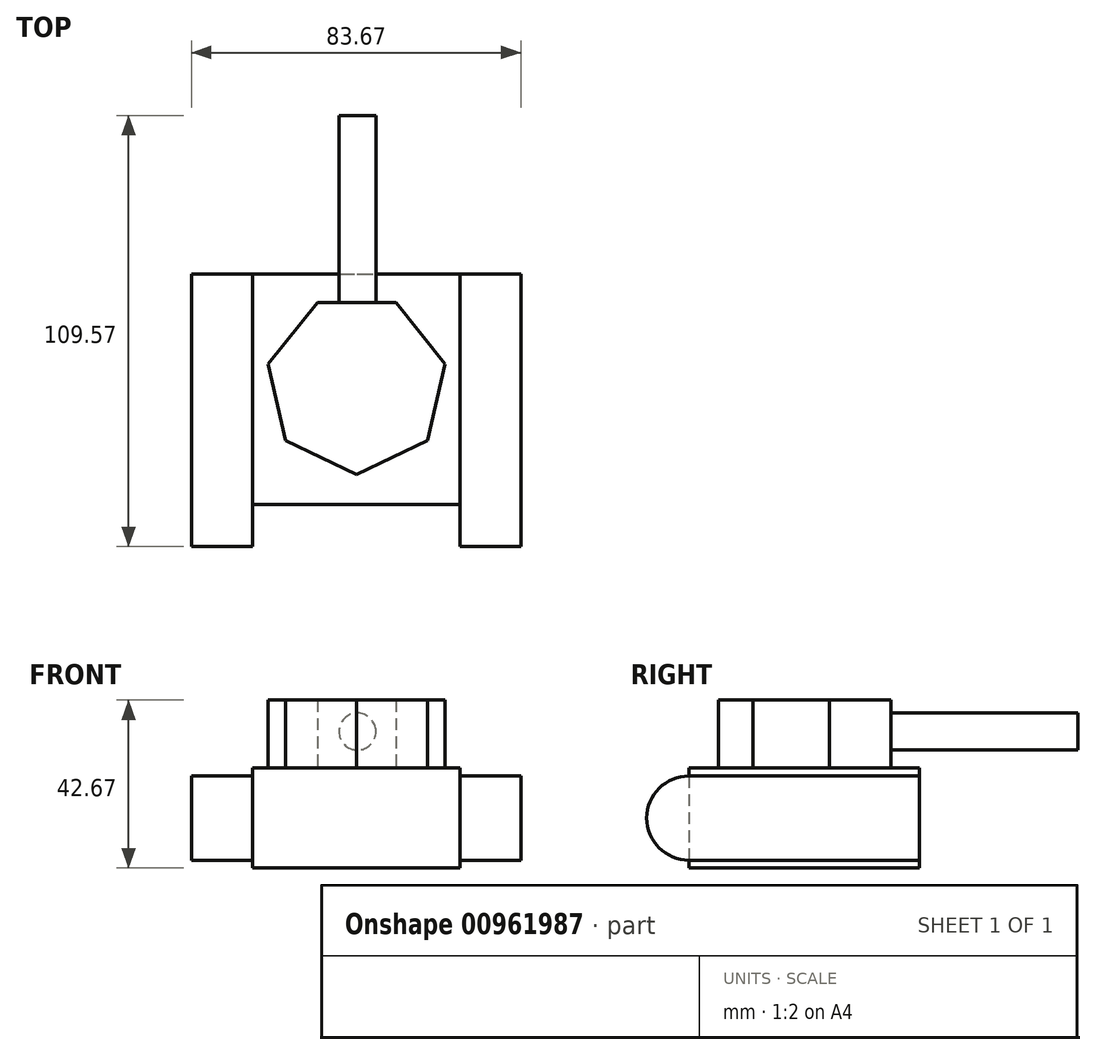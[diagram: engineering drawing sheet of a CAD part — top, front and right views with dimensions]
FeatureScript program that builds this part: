
annotation { "Feature Type Name" : "Feature", "Feature Type Description" : "" }
export const myFeature = defineFeature(function(context is Context, id is Id, definition is map)
    precondition{}
    {
        {
            var Q0;
            Q0=qCreatedBy(makeId("Top.planeOp"),FACE);
            var sketch = newSketch(context, id + "F0", { "sketchPlane" : qUnion([Q0])});
            skLineSegment(sketch, "E0.bottom", {"start": v(-25.12, 27.94) * mm, "end": v(27.57, 27.94) * mm});
            skLineSegment(sketch, "E0.top", {"start": v(-25.12, -30.63) * mm, "end": v(27.57, -30.63) * mm});
            skLineSegment(sketch, "E0.left", {"start": v(-25.12, 27.94) * mm, "end": v(-25.12, -30.63) * mm});
            skLineSegment(sketch, "E0.right", {"start": v(27.57, 27.94) * mm, "end": v(27.57, -30.63) * mm});
            skSolve(sketch);
        }
        {
            var Q0;
            Q0=makeQuery(id+"F0.imprint","IMPRINT",FACE,{"disambiguationData":[TD([[makeQuery(id+"F0.imprint","IMPRINT",EDGE,{"derivedFrom":sQuery(id+"F0.wireOp",EDGE,"E0.bottom")}),-1.0]])]});
            extrude(context, id + "F1", {"entities" : qUnion([Q0]), "depth" : 25.4 * mm, "offsetDistance" : 25.4 * mm});
        }
        {
            var Q0;
            Q0=makeQuery(id+"F1.opExtrude","SWEPT_FACE",FACE,{"disambiguationData":[OSD([sQuery(id+"F0.wireOp",EDGE,"E0.right")])]});
            var sketch = newSketch(context, id + "F2", { "sketchPlane" : qUnion([Q0])});
            skArc(sketch, "E1", {"start": v(-30.63, 23.39) * mm, "mid": v(-41.32, 12.7) * mm, "end": v(-30.63, 2.01) * mm});
            skLineSegment(sketch, "E2", {"start": v(-30.63, 23.39) * mm, "end": v(27.94, 23.39) * mm});
            skLineSegment(sketch, "E3", {"start": v(-30.63, 2.01) * mm, "end": v(27.94, 2.01) * mm});
            skArc(sketch, "E4", {"start": v(27.94, 23.39) * mm, "mid": v(38.62, 12.7) * mm, "end": v(27.94, 2.01) * mm});
            skSolve(sketch);
        }
        {
            var Q0;
            {var subQ0=sQuery(id+"F2.wireOp",EDGE,"E1");Q0=makeQuery(id+"F2.imprint","IMPRINT",FACE,{"disambiguationData":[TD([[makeQuery(id+"F2.imprint","IMPRINT",EDGE,{"derivedFrom":subQ0}),1.0]])]});}
            var Q1;
            {var subQ0=sQuery(id+"F2.wireOp",EDGE,"E2");Q1=makeQuery(id+"F2.imprint","IMPRINT",FACE,{"disambiguationData":[TD([[makeQuery(id+"F2.imprint","IMPRINT",EDGE,{"derivedFrom":subQ0}),-1.0]])]});}
            var Q2;
            {var subQ0=sQuery(id+"F2.wireOp",EDGE,"E4");Q2=makeQuery(id+"F2.imprint","IMPRINT",FACE,{"disambiguationData":[TD([[makeQuery(id+"F2.imprint","IMPRINT",EDGE,{"derivedFrom":subQ0}),-1.0]])]});}
            extrude(context, id + "F3", {"entities" : qUnion([Q0, Q1, Q2]), "depth" : 15.5 * mm, "offsetDistance" : 25.4 * mm});
        }
        {
            var Q0;
            {var subQ2=sQuery(id+"F0.wireOp",EDGE,"E0.right");var subQ5=sQuery(id+"F2.wireOp",EDGE,"E2");Q0=makeQuery(id+"F3.boolean.opBoolean","SPLIT",FACE,{"disambiguationData":[TD([makeQuery(id+"F3.opExtrude","SWEPT_FACE",FACE,{"disambiguationData":[OSD([subQ5])]})])],"derivedFrom":makeQuery(id+"F1.opExtrude","SWEPT_FACE",FACE,{"disambiguationData":[OSD([subQ2])]})});}
            var Q1;
            Q1=makeQuery(id+"F1.opExtrude","SWEPT_FACE",FACE,{"disambiguationData":[OSD([sQuery(id+"F0.wireOp",EDGE,"E0.left")])]});
            cPlane(context, id + "F4", {"entities" : qUnion([Q0, Q1]), "cplaneType" : CPlaneType.MID_PLANE, "offset" : 25.4 * mm, "width" : 152.4 * mm, "height" : 152.4 * mm});
        }
        {
            var Q0;
            Q0=makeQuery(id+"F3.opExtrude","SWEPT_BODY",BODY,{"disambiguationData":[OSD([sQuery(id+"F2.wireOp",EDGE,"E1"),sQuery(id+"F2.wireOp",EDGE,"E2"),sQuery(id+"F2.wireOp",EDGE,"E3"),sQuery(id+"F2.wireOp",EDGE,"E4")])]});
            var Q1;
            Q1=qCreatedBy(id+"F4.planeOp",FACE);
            mirror(context, id + "F5", {"operationType" : NewBodyOperationType.ADD, "entities" : qUnion([Q0]), "mirrorPlane" : qUnion([Q1])});
        }
        {
            var Q0;
            Q0=makeQuery(id+"F1.opExtrude","CAP_FACE",FACE,{"disambiguationData":[OSD([sQuery(id+"F0.wireOp",EDGE,"E0.bottom"),sQuery(id+"F0.wireOp",EDGE,"E0.top"),sQuery(id+"F0.wireOp",EDGE,"E0.left"),sQuery(id+"F0.wireOp",EDGE,"E0.right")])],"isStart":false});
            var sketch = newSketch(context, id + "F6", { "sketchPlane" : qUnion([Q0])});
            skCircle(sketch, "E5.cCircle", {"center": v(1.38, 0) * mm, "radius": 20.75 * mm, "construction": true});
            skLineSegment(sketch, "E5.0", {"start": v(-8.62, 20.75) * mm, "end": v(11.37, 20.75) * mm});
            skLineSegment(sketch, "E5.1", {"start": v(11.37, 20.75) * mm, "end": v(23.83, 5.13) * mm});
            skLineSegment(sketch, "E5.2", {"start": v(23.83, 5.13) * mm, "end": v(19.38, -14.36) * mm});
            skLineSegment(sketch, "E5.3", {"start": v(19.38, -14.36) * mm, "end": v(1.38, -23.03) * mm});
            skLineSegment(sketch, "E5.4", {"start": v(1.38, -23.03) * mm, "end": v(-16.63, -14.36) * mm});
            skLineSegment(sketch, "E5.5", {"start": v(-16.63, -14.36) * mm, "end": v(-21.08, 5.13) * mm});
            skLineSegment(sketch, "E5.6", {"start": v(-21.08, 5.13) * mm, "end": v(-8.62, 20.75) * mm});
            skPoint(sketch, "E5.0.midPoint", {"position": v(1.38, 20.75) * mm});
            skSolve(sketch);
        }
        {
            var Q0;
            Q0=makeQuery(id+"F6.imprint","IMPRINT",FACE,{"disambiguationData":[TD([[makeQuery(id+"F6.imprint","IMPRINT",EDGE,{"derivedFrom":sQuery(id+"F6.wireOp",EDGE,"E5.0")}),-1.0]])]});
            extrude(context, id + "F7", {"entities" : qUnion([Q0]), "operationType" : NewBodyOperationType.ADD, "depth" : 17.27 * mm, "offsetDistance" : 25.4 * mm});
        }
        {
            var Q0;
            Q0=makeQuery(id+"F7.opExtrude","SWEPT_FACE",FACE,{"disambiguationData":[OSD([sQuery(id+"F6.wireOp",EDGE,"E5.0")])]});
            var sketch = newSketch(context, id + "F8", { "sketchPlane" : qUnion([Q0])});
            skCircle(sketch, "E6", {"center": v(-1.56, 34.7) * mm, "radius": 4.7 * mm});
            skSolve(sketch);
        }
        {
            var Q0;
            Q0=makeQuery(id+"F8.imprint","IMPRINT",FACE,{"disambiguationData":[TD([[makeQuery(id+"F8.imprint","IMPRINT",EDGE,{"derivedFrom":sQuery(id+"F8.wireOp",EDGE,"E6")}),1.0]])]});
            extrude(context, id + "F9", {"entities" : qUnion([Q0]), "operationType" : NewBodyOperationType.ADD, "depth" : 47.5 * mm, "offsetDistance" : 25.4 * mm});
        }
    });
